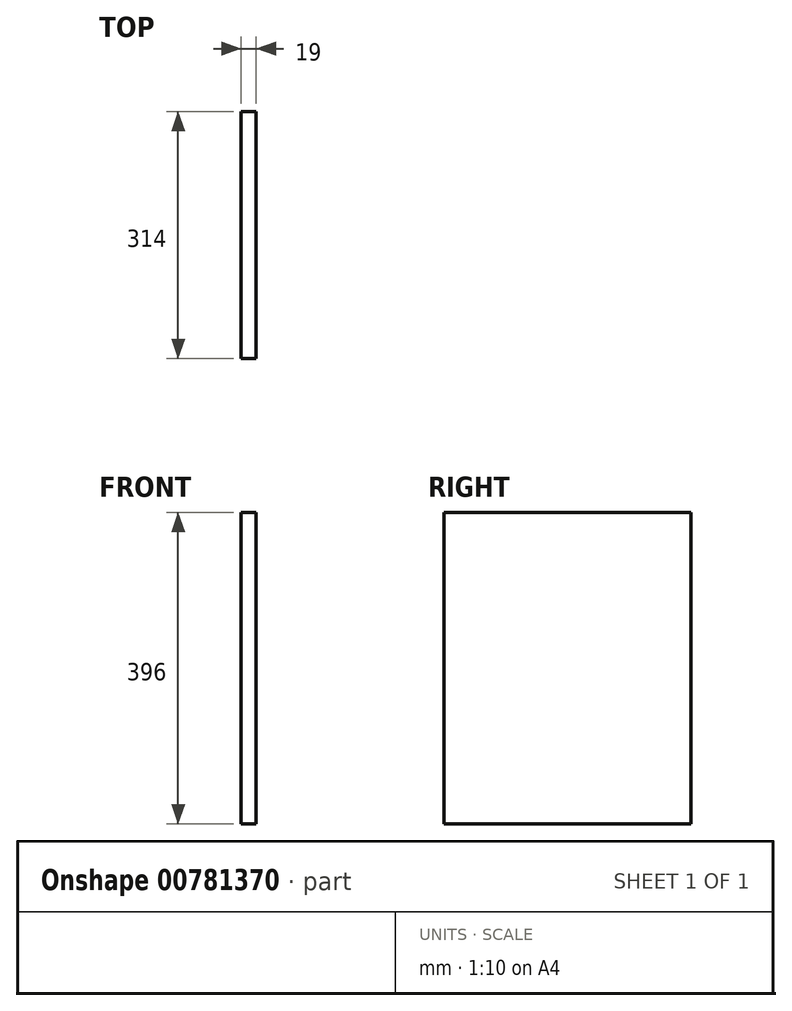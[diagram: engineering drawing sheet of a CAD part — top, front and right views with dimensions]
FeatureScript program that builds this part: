
annotation { "Feature Type Name" : "Feature", "Feature Type Description" : "" }
export const myFeature = defineFeature(function(context is Context, id is Id, definition is map)
    precondition{}
    {
        {
            var Q0;
            Q0=qCreatedBy(makeId("Right.planeOp"),FACE);
            var sketch = newSketch(context, id + "F0", { "sketchPlane" : qUnion([Q0])});
            skLineSegment(sketch, "E0.bottom", {"start": v(157, -198) * mm, "end": v(-157, -198) * mm});
            skLineSegment(sketch, "E0.top", {"start": v(157, 198) * mm, "end": v(-157, 198) * mm});
            skLineSegment(sketch, "E0.left", {"start": v(157, -198) * mm, "end": v(157, 198) * mm});
            skLineSegment(sketch, "E0.right", {"start": v(-157, -198) * mm, "end": v(-157, 198) * mm});
            skPoint(sketch, "E0.middle", {"position": v(0, 0) * mm});
            skSolve(sketch);
        }
        {
            var Q0;
            Q0=qSketchRegion(id+"F0",true);
            extrude(context, id + "F1", {"entities" : qUnion([Q0]), "depth" : 19 * mm, "offsetDistance" : 25.4 * mm});
        }
    });
